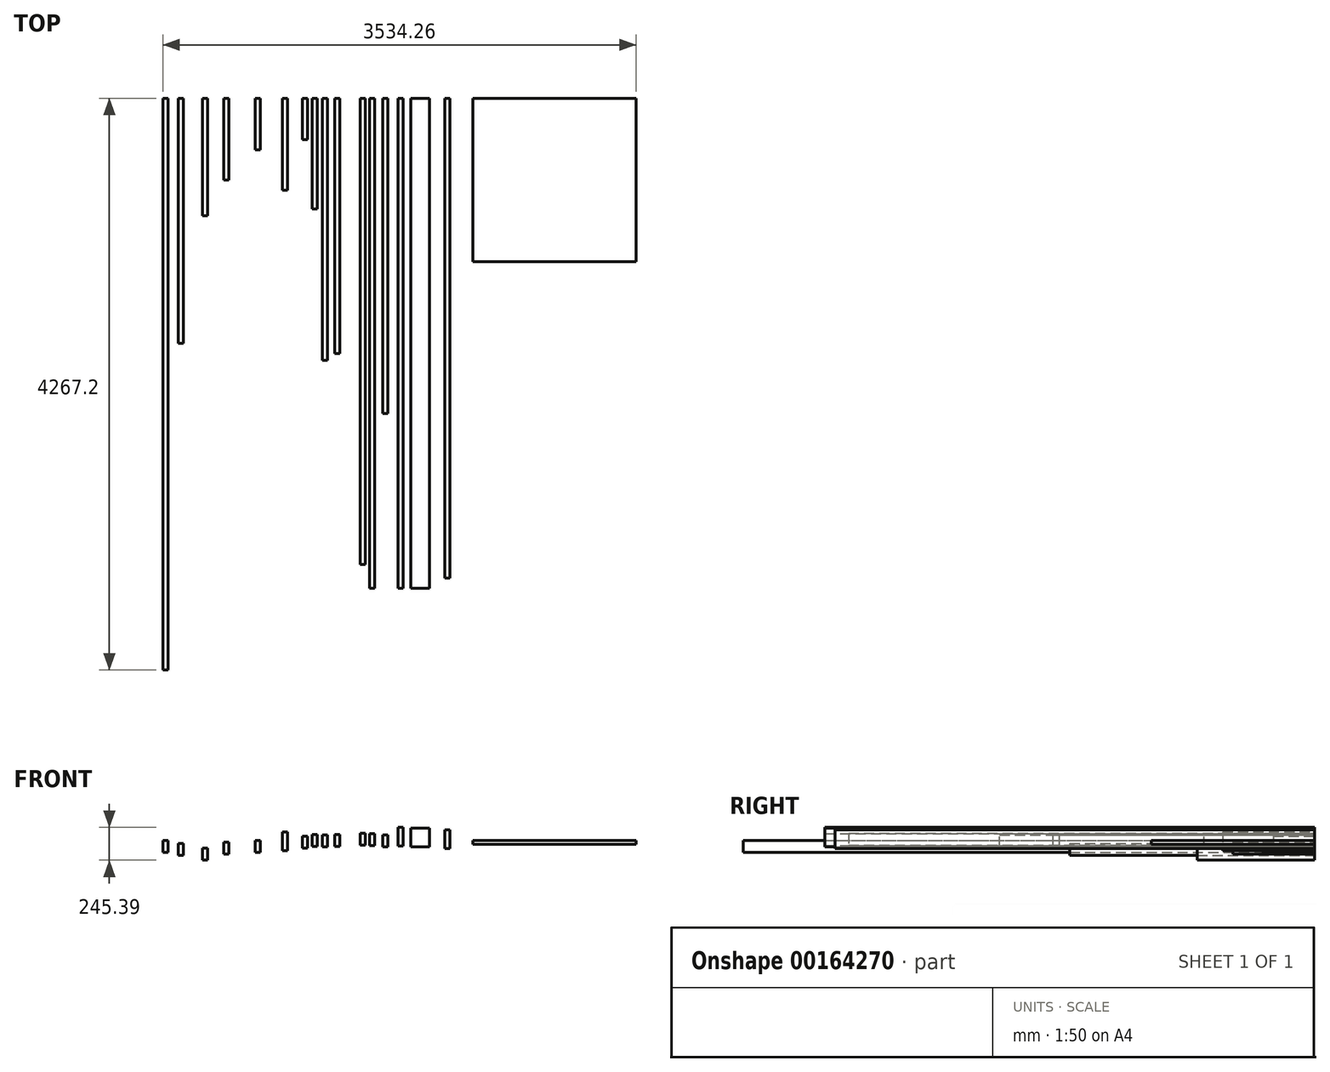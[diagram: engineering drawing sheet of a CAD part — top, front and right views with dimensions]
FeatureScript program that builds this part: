
annotation { "Feature Type Name" : "Feature", "Feature Type Description" : "" }
export const myFeature = defineFeature(function(context is Context, id is Id, definition is map)
    precondition{}
    {
        {
            var Q0;
            Q0=qCreatedBy(makeId("Front.planeOp"),FACE);
            var sketch = newSketch(context, id + "F0", { "sketchPlane" : qUnion([Q0])});
            skLineSegment(sketch, "E0.bottom", {"start": v(-345.5, 99.38) * mm, "end": v(-307.4, 99.38) * mm});
            skLineSegment(sketch, "E0.top", {"start": v(-345.5, -40.32) * mm, "end": v(-307.4, -40.32) * mm});
            skLineSegment(sketch, "E0.left", {"start": v(-345.5, 99.38) * mm, "end": v(-345.5, -40.32) * mm});
            skLineSegment(sketch, "E0.right", {"start": v(-307.4, 99.38) * mm, "end": v(-307.4, -40.32) * mm});
            skSolve(sketch);
        }
        {
            var Q0;
            Q0=makeQuery(id+"F0.imprint","IMPRINT",FACE,{"disambiguationData":[TD([[makeQuery(id+"F0.imprint","IMPRINT",EDGE,{"derivedFrom":sQuery(id+"F0.wireOp",EDGE,"E0.bottom")}),-1.0]])]});
            extrude(context, id + "F1", {"entities" : qUnion([Q0]), "depth" : 3657.6 * mm});
        }
        {
            var Q0;
            Q0=qCreatedBy(makeId("Front.planeOp"),FACE);
            var sketch = newSketch(context, id + "F2", { "sketchPlane" : qUnion([Q0])});
            skLineSegment(sketch, "E1.bottom", {"start": v(-251.58, 91.94) * mm, "end": v(-111.88, 91.94) * mm});
            skLineSegment(sketch, "E1.top", {"start": v(-251.58, -47.76) * mm, "end": v(-111.88, -47.76) * mm});
            skLineSegment(sketch, "E1.left", {"start": v(-251.58, 91.94) * mm, "end": v(-251.58, -47.76) * mm});
            skLineSegment(sketch, "E1.right", {"start": v(-111.88, 91.94) * mm, "end": v(-111.88, -47.76) * mm});
            skSolve(sketch);
        }
        {
            var Q0;
            Q0=makeQuery(id+"F2.imprint","IMPRINT",FACE,{"disambiguationData":[TD([[makeQuery(id+"F2.imprint","IMPRINT",EDGE,{"derivedFrom":sQuery(id+"F2.wireOp",EDGE,"E1.bottom")}),-1.0]])]});
            extrude(context, id + "F3", {"entities" : qUnion([Q0]), "depth" : 3657.6 * mm});
        }
        {
            var Q0;
            Q0=makeQuery(id+"F1.opExtrude","SWEPT_FACE",FACE,{"disambiguationData":[OSD([sQuery(id+"F0.wireOp",EDGE,"E0.top")])]});
            var sketch = newSketch(context, id + "F4", { "sketchPlane" : qUnion([Q0])});
            skLineSegment(sketch, "E2", {"start": v(-307.66, 19.05) * mm, "end": v(-345.5, 19.05) * mm});
            skLineSegment(sketch, "E3.0.1.0", {"start": v(-307.66, 387.35) * mm, "end": v(-345.5, 387.35) * mm});
            skLineSegment(sketch, "E3.0.2.0", {"start": v(-307.66, 755.65) * mm, "end": v(-345.5, 755.65) * mm});
            skLineSegment(sketch, "E3.0.3.0", {"start": v(-307.66, 1123.95) * mm, "end": v(-345.5, 1123.95) * mm});
            skLineSegment(sketch, "E3.0.4.0", {"start": v(-307.66, 1492.25) * mm, "end": v(-345.5, 1492.25) * mm});
            skLineSegment(sketch, "E3.0.5.0", {"start": v(-307.66, 1860.55) * mm, "end": v(-345.5, 1860.55) * mm});
            skLineSegment(sketch, "E3.0.6.0", {"start": v(-307.66, 2228.85) * mm, "end": v(-345.5, 2228.85) * mm});
            skLineSegment(sketch, "E3.0.7.0", {"start": v(-307.66, 2597.15) * mm, "end": v(-345.5, 2597.15) * mm});
            skLineSegment(sketch, "E3.0.8.0", {"start": v(-307.66, 2965.45) * mm, "end": v(-345.5, 2965.45) * mm});
            skLineSegment(sketch, "E3.0.9.0", {"start": v(-307.66, 3333.75) * mm, "end": v(-345.5, 3333.75) * mm});
            skLineSegment(sketch, "E3.direction1", {"start": v(-345.5, 19.05) * mm, "end": v(-320.1, 19.05) * mm, "construction": true});
            skLineSegment(sketch, "E3.direction2", {"start": v(-345.5, 19.05) * mm, "end": v(-345.5, 387.35) * mm, "construction": true});
            skSolve(sketch);
        }
        {
            var Q0;
            Q0=qCreatedBy(makeId("Front.planeOp"),FACE);
            var sketch = newSketch(context, id + "F5", { "sketchPlane" : qUnion([Q0])});
            skLineSegment(sketch, "E4.bottom", {"start": v(4.4, 79.67) * mm, "end": v(42.5, 79.67) * mm});
            skLineSegment(sketch, "E4.top", {"start": v(4.4, -60.03) * mm, "end": v(42.5, -60.03) * mm});
            skLineSegment(sketch, "E4.left", {"start": v(4.4, 79.67) * mm, "end": v(4.4, -60.03) * mm});
            skLineSegment(sketch, "E4.right", {"start": v(42.5, 79.67) * mm, "end": v(42.5, -60.03) * mm});
            skSolve(sketch);
        }
        {
            var Q0;
            Q0=makeQuery(id+"F5.imprint","IMPRINT",FACE,{"disambiguationData":[TD([[makeQuery(id+"F5.imprint","IMPRINT",EDGE,{"derivedFrom":sQuery(id+"F5.wireOp",EDGE,"E4.bottom")}),-1.0]])]});
            extrude(context, id + "F6", {"entities" : qUnion([Q0]), "depth" : 3581.4 * mm});
        }
        {
            var Q0;
            Q0=makeQuery(id+"F6.opExtrude","SWEPT_FACE",FACE,{"disambiguationData":[OSD([sQuery(id+"F5.wireOp",EDGE,"E4.top")])]});
            var sketch = newSketch(context, id + "F7", { "sketchPlane" : qUnion([Q0])});
            skLineSegment(sketch, "E5", {"start": v(42.5, 3543.3) * mm, "end": v(4.4, 3543.3) * mm});
            skLineSegment(sketch, "E6.0.1.0", {"start": v(42.5, 2657.48) * mm, "end": v(4.4, 2657.48) * mm});
            skLineSegment(sketch, "E6.0.2.0", {"start": v(42.5, 1771.65) * mm, "end": v(4.4, 1771.65) * mm});
            skLineSegment(sketch, "E6.0.3.0", {"start": v(42.5, 885.83) * mm, "end": v(4.4, 885.83) * mm});
            skLineSegment(sketch, "E6.0.4.0", {"start": v(42.5, 0) * mm, "end": v(4.4, 0) * mm});
            skLineSegment(sketch, "E6.direction1", {"start": v(4.4, 3543.3) * mm, "end": v(29.8, 3543.3) * mm, "construction": true});
            skLineSegment(sketch, "E6.direction2", {"start": v(4.4, 3543.3) * mm, "end": v(4.4, 2657.48) * mm, "construction": true});
            skSolve(sketch);
        }
        {
            var Q0;
            Q0=qCreatedBy(makeId("Front.planeOp"),FACE);
            var sketch = newSketch(context, id + "F8", { "sketchPlane" : qUnion([Q0])});
            skLineSegment(sketch, "E7.bottom", {"start": v(212.9, -26.47) * mm, "end": v(1432.1, -26.47) * mm});
            skLineSegment(sketch, "E7.top", {"start": v(212.9, 2.1) * mm, "end": v(1432.1, 2.1) * mm});
            skLineSegment(sketch, "E7.left", {"start": v(212.9, -26.47) * mm, "end": v(212.9, 2.1) * mm});
            skLineSegment(sketch, "E7.right", {"start": v(1432.1, -26.47) * mm, "end": v(1432.1, 2.1) * mm});
            skSolve(sketch);
        }
        {
            var Q0;
            Q0=makeQuery(id+"F8.imprint","IMPRINT",FACE,{"disambiguationData":[TD([[makeQuery(id+"F8.imprint","IMPRINT",EDGE,{"derivedFrom":sQuery(id+"F8.wireOp",EDGE,"E7.bottom")}),1.0]])]});
            extrude(context, id + "F9", {"entities" : qUnion([Q0]), "depth" : 1219.2 * mm});
        }
        {
            var Q0;
            Q0=qCreatedBy(makeId("Front.planeOp"),FACE);
            var sketch = newSketch(context, id + "F10", { "sketchPlane" : qUnion([Q0])});
            skLineSegment(sketch, "E8.bottom", {"start": v(-421.25, -46.7) * mm, "end": v(-459.35, -46.7) * mm});
            skLineSegment(sketch, "E8.top", {"start": v(-421.25, 42.2) * mm, "end": v(-459.35, 42.2) * mm});
            skLineSegment(sketch, "E8.left", {"start": v(-421.25, -46.7) * mm, "end": v(-421.25, 42.2) * mm});
            skLineSegment(sketch, "E8.right", {"start": v(-459.35, -46.7) * mm, "end": v(-459.35, 42.2) * mm});
            skSolve(sketch);
        }
        {
            var Q0;
            Q0 = qSketchRegion(id + "F10", true);
            extrude(context, id + "F11", {"entities" : qUnion([Q0]), "depth" : 2352.67 * mm});
        }
        {
            var Q0;
            Q0=qCreatedBy(makeId("Front.planeOp"),FACE);
            var sketch = newSketch(context, id + "F12", { "sketchPlane" : qUnion([Q0])});
            skLineSegment(sketch, "E9.bottom", {"start": v(-522.1, -36.22) * mm, "end": v(-560.2, -36.22) * mm});
            skLineSegment(sketch, "E9.top", {"start": v(-522.1, 52.68) * mm, "end": v(-560.2, 52.68) * mm});
            skLineSegment(sketch, "E9.left", {"start": v(-522.1, -36.22) * mm, "end": v(-522.1, 52.68) * mm});
            skLineSegment(sketch, "E9.right", {"start": v(-560.2, -36.22) * mm, "end": v(-560.2, 52.68) * mm});
            skSolve(sketch);
        }
        {
            var Q0;
            Q0 = qSketchRegion(id + "F12", true);
            extrude(context, id + "F13", {"entities" : qUnion([Q0]), "depth" : 3657.6 * mm});
        }
        {
            var Q0;
            Q0=makeQuery(id+"F13.opExtrude","SWEPT_FACE",FACE,{"disambiguationData":[OSD([sQuery(id+"F12.wireOp",EDGE,"E9.left")])]});
            var sketch = newSketch(context, id + "F14", { "sketchPlane" : qUnion([Q0])});
            skLineSegment(sketch, "E10", {"start": v(-3638.55, 52.68) * mm, "end": v(-3638.55, -36.22) * mm});
            skLineSegment(sketch, "E11.1.0.0", {"start": v(-3232.15, 52.68) * mm, "end": v(-3232.15, -36.22) * mm});
            skLineSegment(sketch, "E11.2.0.0", {"start": v(-2825.75, 52.68) * mm, "end": v(-2825.75, -36.22) * mm});
            skLineSegment(sketch, "E11.3.0.0", {"start": v(-2419.35, 52.68) * mm, "end": v(-2419.35, -36.22) * mm});
            skLineSegment(sketch, "E11.4.0.0", {"start": v(-2012.95, 52.68) * mm, "end": v(-2012.95, -36.22) * mm});
            skLineSegment(sketch, "E11.5.0.0", {"start": v(-1606.55, 52.68) * mm, "end": v(-1606.55, -36.22) * mm});
            skLineSegment(sketch, "E11.6.0.0", {"start": v(-1200.15, 52.68) * mm, "end": v(-1200.15, -36.22) * mm});
            skLineSegment(sketch, "E11.7.0.0", {"start": v(-793.75, 52.68) * mm, "end": v(-793.75, -36.22) * mm});
            skLineSegment(sketch, "E11.8.0.0", {"start": v(-387.35, 52.68) * mm, "end": v(-387.35, -36.22) * mm});
            skLineSegment(sketch, "E11.direction1", {"start": v(-3638.55, -36.22) * mm, "end": v(-3232.15, -36.22) * mm, "construction": true});
            skSolve(sketch);
        }
        {
            var Q0;
            Q0=qCreatedBy(makeId("Front.planeOp"),FACE);
            var sketch = newSketch(context, id + "F15", { "sketchPlane" : qUnion([Q0])});
            skLineSegment(sketch, "E12.bottom", {"start": v(-627.56, 54.4) * mm, "end": v(-589.46, 54.4) * mm});
            skLineSegment(sketch, "E12.top", {"start": v(-627.56, -34.5) * mm, "end": v(-589.46, -34.5) * mm});
            skLineSegment(sketch, "E12.left", {"start": v(-627.56, 54.4) * mm, "end": v(-627.56, -34.5) * mm});
            skLineSegment(sketch, "E12.right", {"start": v(-589.46, 54.4) * mm, "end": v(-589.46, -34.5) * mm});
            skSolve(sketch);
        }
        {
            var Q0;
            Q0 = qSketchRegion(id + "F15", true);
            extrude(context, id + "F16", {"entities" : qUnion([Q0]), "depth" : 3479.8 * mm});
        }
        {
            var Q0;
            Q0=makeQuery(id+"F16.opExtrude","SWEPT_FACE",FACE,{"disambiguationData":[OSD([sQuery(id+"F15.wireOp",EDGE,"E12.right")])]});
            var sketch = newSketch(context, id + "F17", { "sketchPlane" : qUnion([Q0])});
            skLineSegment(sketch, "E13.left", {"start": v(-3479.8, -34.5) * mm, "end": v(-3479.8, 54.4) * mm});
            skLineSegment(sketch, "E13.right", {"start": v(-3130.55, -34.5) * mm, "end": v(-3130.55, 54.4) * mm});
            skLineSegment(sketch, "E14.1.0.0", {"start": v(-2724.15, -34.5) * mm, "end": v(-2724.15, 54.4) * mm});
            skLineSegment(sketch, "E14.2.0.0", {"start": v(-2317.75, -34.5) * mm, "end": v(-2317.75, 54.4) * mm});
            skLineSegment(sketch, "E14.3.0.0", {"start": v(-1911.35, -34.5) * mm, "end": v(-1911.35, 54.4) * mm});
            skLineSegment(sketch, "E14.4.0.0", {"start": v(-1504.95, -34.5) * mm, "end": v(-1504.95, 54.4) * mm});
            skLineSegment(sketch, "E14.5.0.0", {"start": v(-1098.55, -34.5) * mm, "end": v(-1098.55, 54.4) * mm});
            skLineSegment(sketch, "E14.6.0.0", {"start": v(-692.15, -34.5) * mm, "end": v(-692.15, 54.4) * mm});
            skLineSegment(sketch, "E14.7.0.0", {"start": v(-285.75, -34.5) * mm, "end": v(-285.75, 54.4) * mm});
            skLineSegment(sketch, "E14.direction1", {"start": v(-3130.55, -34.5) * mm, "end": v(-2724.15, -34.5) * mm, "construction": true});
            skLineSegment(sketch, "E15", {"start": v(-88.9, -34.5) * mm, "end": v(-88.9, 54.4) * mm});
            skSolve(sketch);
        }
        {
            var Q0;
            Q0=qCreatedBy(makeId("Front.planeOp"),FACE);
            var sketch = newSketch(context, id + "F18", { "sketchPlane" : qUnion([Q0])});
            skLineSegment(sketch, "E16.bottom", {"start": v(-909.9, 41.1) * mm, "end": v(-871.8, 41.1) * mm});
            skLineSegment(sketch, "E16.top", {"start": v(-909.9, -47.8) * mm, "end": v(-871.8, -47.8) * mm});
            skLineSegment(sketch, "E16.left", {"start": v(-909.9, 41.1) * mm, "end": v(-909.9, -47.8) * mm});
            skLineSegment(sketch, "E16.right", {"start": v(-871.8, 41.1) * mm, "end": v(-871.8, -47.8) * mm});
            skSolve(sketch);
        }
        {
            var Q0;
            Q0 = qSketchRegion(id + "F18", true);
            extrude(context, id + "F19", {"entities" : qUnion([Q0]), "depth" : 1955.8 * mm});
        }
        {
            var Q0;
            Q0=qCreatedBy(makeId("Front.planeOp"),FACE);
            var sketch = newSketch(context, id + "F20", { "sketchPlane" : qUnion([Q0])});
            skLineSegment(sketch, "E17.bottom", {"start": v(-780.58, -43.25) * mm, "end": v(-818.68, -43.25) * mm});
            skLineSegment(sketch, "E17.top", {"start": v(-780.58, 45.65) * mm, "end": v(-818.68, 45.65) * mm});
            skLineSegment(sketch, "E17.left", {"start": v(-780.58, -43.25) * mm, "end": v(-780.58, 45.65) * mm});
            skLineSegment(sketch, "E17.right", {"start": v(-818.68, -43.25) * mm, "end": v(-818.68, 45.65) * mm});
            skSolve(sketch);
        }
        {
            var Q0;
            Q0 = qSketchRegion(id + "F20", true);
            extrude(context, id + "F21", {"entities" : qUnion([Q0]), "depth" : 1905 * mm});
        }
        {
            var Q0;
            Q0=qCreatedBy(makeId("Front.planeOp"),FACE);
            var sketch = newSketch(context, id + "F22", { "sketchPlane" : qUnion([Q0])});
            skLineSegment(sketch, "E18.bottom", {"start": v(-949.33, -44) * mm, "end": v(-987.43, -44) * mm});
            skLineSegment(sketch, "E18.top", {"start": v(-949.33, 44.9) * mm, "end": v(-987.43, 44.9) * mm});
            skLineSegment(sketch, "E18.left", {"start": v(-949.33, -44) * mm, "end": v(-949.33, 44.9) * mm});
            skLineSegment(sketch, "E18.right", {"start": v(-987.43, -44) * mm, "end": v(-987.43, 44.9) * mm});
            skSolve(sketch);
        }
        {
            var Q0;
            Q0 = qSketchRegion(id + "F22", true);
            extrude(context, id + "F23", {"entities" : qUnion([Q0]), "depth" : 825.5 * mm});
        }
        {
            var Q0;
            Q0=qCreatedBy(makeId("Front.planeOp"),FACE);
            var sketch = newSketch(context, id + "F24", { "sketchPlane" : qUnion([Q0])});
            skLineSegment(sketch, "E19.bottom", {"start": v(-1059.28, 32.74) * mm, "end": v(-1021.18, 32.74) * mm});
            skLineSegment(sketch, "E19.top", {"start": v(-1059.28, -56.16) * mm, "end": v(-1021.18, -56.16) * mm});
            skLineSegment(sketch, "E19.left", {"start": v(-1059.28, 32.74) * mm, "end": v(-1059.28, -56.16) * mm});
            skLineSegment(sketch, "E19.right", {"start": v(-1021.18, 32.74) * mm, "end": v(-1021.18, -56.16) * mm});
            skSolve(sketch);
        }
        {
            var Q0;
            Q0 = qSketchRegion(id + "F24", true);
            extrude(context, id + "F25", {"entities" : qUnion([Q0]), "depth" : 307.97 * mm});
        }
        {
            var Q0;
            Q0=makeQuery(id+"F16.opExtrude","SWEPT_FACE",FACE,{"disambiguationData":[OSD([sQuery(id+"F15.wireOp",EDGE,"E12.left")])]});
            var sketch = newSketch(context, id + "F26", { "sketchPlane" : qUnion([Q0])});
            skLineSegment(sketch, "E20", {"start": v(3181.35, 54.4) * mm, "end": v(3181.35, -34.5) * mm});
            skLineSegment(sketch, "E21.1.0.0", {"start": v(2774.95, 54.4) * mm, "end": v(2774.95, -34.5) * mm});
            skLineSegment(sketch, "E21.2.0.0", {"start": v(2368.55, 54.4) * mm, "end": v(2368.55, -34.5) * mm});
            skLineSegment(sketch, "E21.3.0.0", {"start": v(1962.15, 54.4) * mm, "end": v(1962.15, -34.5) * mm});
            skLineSegment(sketch, "E21.4.0.0", {"start": v(1555.75, 54.4) * mm, "end": v(1555.75, -34.5) * mm});
            skLineSegment(sketch, "E21.5.0.0", {"start": v(1149.35, 54.4) * mm, "end": v(1149.35, -34.5) * mm});
            skLineSegment(sketch, "E21.6.0.0", {"start": v(742.95, 54.4) * mm, "end": v(742.95, -34.5) * mm});
            skLineSegment(sketch, "E21.7.0.0", {"start": v(336.55, 54.4) * mm, "end": v(336.55, -34.5) * mm});
            skLineSegment(sketch, "E21.direction1", {"start": v(3181.35, -34.5) * mm, "end": v(2774.95, -34.5) * mm, "construction": true});
            skSolve(sketch);
        }
        {
            var Q0;
            Q0=qCreatedBy(makeId("Front.planeOp"),FACE);
            var sketch = newSketch(context, id + "F27", { "sketchPlane" : qUnion([Q0])});
            skLineSegment(sketch, "E22.bottom", {"start": v(-1170.79, 65.02) * mm, "end": v(-1208.89, 65.02) * mm});
            skLineSegment(sketch, "E22.top", {"start": v(-1170.79, -74.68) * mm, "end": v(-1208.89, -74.68) * mm});
            skLineSegment(sketch, "E22.left", {"start": v(-1170.79, 65.02) * mm, "end": v(-1170.79, -74.68) * mm});
            skLineSegment(sketch, "E22.right", {"start": v(-1208.89, 65.02) * mm, "end": v(-1208.89, -74.68) * mm});
            skSolve(sketch);
        }
        {
            var Q0;
            Q0 = qSketchRegion(id + "F27", true);
            extrude(context, id + "F28", {"entities" : qUnion([Q0]), "depth" : 685.8 * mm});
        }
        {
            var Q0;
            Q0=qCreatedBy(makeId("Front.planeOp"),FACE);
            var sketch = newSketch(context, id + "F29", { "sketchPlane" : qUnion([Q0])});
            skLineSegment(sketch, "E23.bottom", {"start": v(-1413.36, 2.46) * mm, "end": v(-1375.26, 2.46) * mm});
            skLineSegment(sketch, "E23.top", {"start": v(-1413.36, -86.44) * mm, "end": v(-1375.26, -86.44) * mm});
            skLineSegment(sketch, "E23.left", {"start": v(-1413.36, 2.46) * mm, "end": v(-1413.36, -86.44) * mm});
            skLineSegment(sketch, "E23.right", {"start": v(-1375.26, 2.46) * mm, "end": v(-1375.26, -86.44) * mm});
            skSolve(sketch);
        }
        {
            var Q0;
            Q0 = qSketchRegion(id + "F29", true);
            extrude(context, id + "F30", {"entities" : qUnion([Q0]), "depth" : 384.17 * mm});
        }
        {
            var Q0;
            Q0=qCreatedBy(makeId("Front.planeOp"),FACE);
            var sketch = newSketch(context, id + "F31", { "sketchPlane" : qUnion([Q0])});
            skLineSegment(sketch, "E24.bottom", {"start": v(-1609.26, -11.92) * mm, "end": v(-1647.36, -11.92) * mm});
            skLineSegment(sketch, "E24.top", {"start": v(-1609.26, -100.82) * mm, "end": v(-1647.36, -100.82) * mm});
            skLineSegment(sketch, "E24.left", {"start": v(-1609.26, -11.92) * mm, "end": v(-1609.26, -100.82) * mm});
            skLineSegment(sketch, "E24.right", {"start": v(-1647.36, -11.92) * mm, "end": v(-1647.36, -100.82) * mm});
            skSolve(sketch);
        }
        {
            var Q0;
            Q0 = qSketchRegion(id + "F31", true);
            extrude(context, id + "F32", {"entities" : qUnion([Q0]), "depth" : 609.6 * mm});
        }
        {
            var Q0;
            Q0=qCreatedBy(makeId("Front.planeOp"),FACE);
            var sketch = newSketch(context, id + "F33", { "sketchPlane" : qUnion([Q0])});
            skLineSegment(sketch, "E25.bottom", {"start": v(-1769.65, -57.11) * mm, "end": v(-1807.75, -57.11) * mm});
            skLineSegment(sketch, "E25.top", {"start": v(-1769.65, -146.01) * mm, "end": v(-1807.75, -146.01) * mm});
            skLineSegment(sketch, "E25.left", {"start": v(-1769.65, -57.11) * mm, "end": v(-1769.65, -146.01) * mm});
            skLineSegment(sketch, "E25.right", {"start": v(-1807.75, -57.11) * mm, "end": v(-1807.75, -146.01) * mm});
            skSolve(sketch);
        }
        {
            var Q0;
            Q0 = qSketchRegion(id + "F33", true);
            extrude(context, id + "F34", {"entities" : qUnion([Q0]), "depth" : 876.3 * mm});
        }
        {
            var Q0;
            Q0=qCreatedBy(makeId("Front.planeOp"),FACE);
            var sketch = newSketch(context, id + "F35", { "sketchPlane" : qUnion([Q0])});
            skLineSegment(sketch, "E26.bottom", {"start": v(-1948.66, -19.51) * mm, "end": v(-1986.76, -19.51) * mm});
            skLineSegment(sketch, "E26.top", {"start": v(-1948.66, -108.41) * mm, "end": v(-1986.76, -108.41) * mm});
            skLineSegment(sketch, "E26.left", {"start": v(-1948.66, -19.51) * mm, "end": v(-1948.66, -108.41) * mm});
            skLineSegment(sketch, "E26.right", {"start": v(-1986.76, -19.51) * mm, "end": v(-1986.76, -108.41) * mm});
            skSolve(sketch);
        }
        {
            var Q0;
            Q0=makeQuery(id+"F35.imprint","IMPRINT",FACE,{"disambiguationData":[TD([[makeQuery(id+"F35.imprint","IMPRINT",EDGE,{"derivedFrom":sQuery(id+"F35.wireOp",EDGE,"E26.bottom")}),1.0]])]});
            extrude(context, id + "F36", {"entities" : qUnion([Q0]), "depth" : 1828.8 * mm});
        }
        {
            var Q0;
            Q0=qCreatedBy(makeId("Front.planeOp"),FACE);
            var sketch = newSketch(context, id + "F37", { "sketchPlane" : qUnion([Q0])});
            skLineSegment(sketch, "E27.bottom", {"start": v(-2064.06, 0) * mm, "end": v(-2102.16, 0) * mm});
            skLineSegment(sketch, "E27.top", {"start": v(-2064.06, -88.9) * mm, "end": v(-2102.16, -88.9) * mm});
            skLineSegment(sketch, "E27.left", {"start": v(-2064.06, 0) * mm, "end": v(-2064.06, -88.9) * mm});
            skLineSegment(sketch, "E27.right", {"start": v(-2102.16, 0) * mm, "end": v(-2102.16, -88.9) * mm});
            skSolve(sketch);
        }
        {
            var Q0;
            Q0=makeQuery(id+"F37.imprint","IMPRINT",FACE,{"disambiguationData":[TD([[makeQuery(id+"F37.imprint","IMPRINT",EDGE,{"derivedFrom":sQuery(id+"F37.wireOp",EDGE,"E27.bottom")}),1.0]])]});
            extrude(context, id + "F38", {"entities" : qUnion([Q0]), "depth" : 4267.2 * mm});
        }
    });
